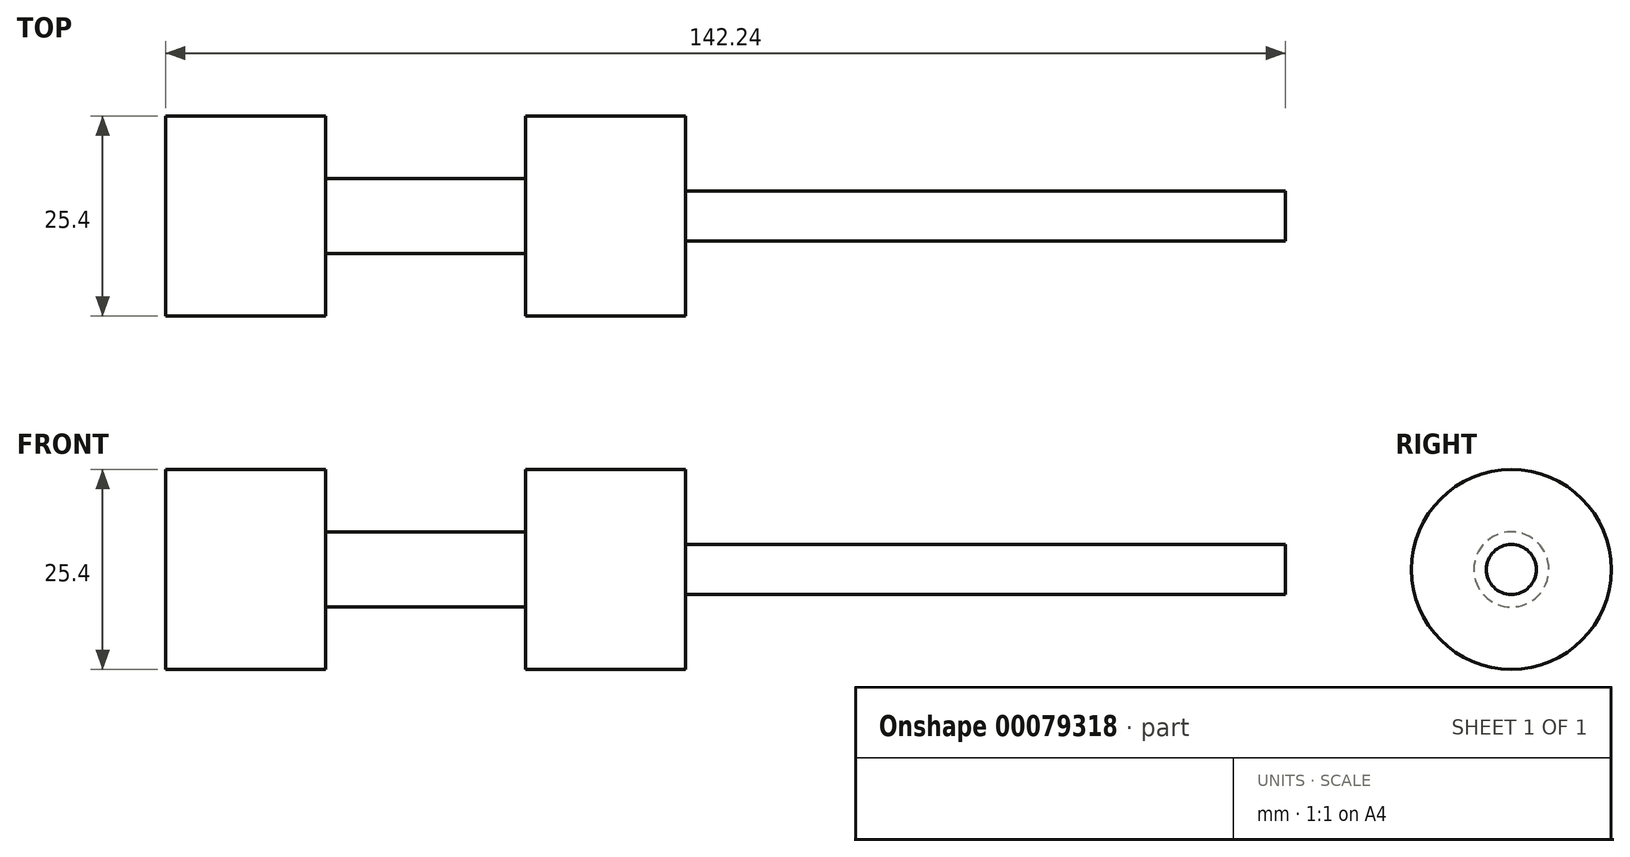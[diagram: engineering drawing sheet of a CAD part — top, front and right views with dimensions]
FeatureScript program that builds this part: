
annotation { "Feature Type Name" : "Feature", "Feature Type Description" : "" }
export const myFeature = defineFeature(function(context is Context, id is Id, definition is map)
    precondition{}
    {
        {
            var Q0;
            Q0=qCreatedBy(makeId("Right.planeOp"),FACE);
            var sketch = newSketch(context, id + "F0", { "sketchPlane" : qUnion([Q0])});
            skCircle(sketch, "E0", {"center": v(0, 0) * mm, "radius": 4.76 * mm});
            skSolve(sketch);
        }
        {
            var Q0;
            Q0 = qSketchRegion(id + "F0", true);
            extrude(context, id + "F1", {"entities" : qUnion([Q0]), "depth" : 12.7 * mm});
        }
        {
            var Q0;
            Q0=makeQuery(id+"F1.opExtrude","CAP_FACE",FACE,{"disambiguationData":[OSD([sQuery(id+"F0.wireOp",EDGE,"E0")])],"isStart":false});
            var sketch = newSketch(context, id + "F2", { "sketchPlane" : qUnion([Q0])});
            skCircle(sketch, "E1", {"center": v(0, 0) * mm, "radius": 12.7 * mm});
            skSolve(sketch);
        }
        {
            var Q0;
            Q0 = qSketchRegion(id + "F2", true);
            extrude(context, id + "F3", {"entities" : qUnion([Q0]), "operationType" : NewBodyOperationType.ADD, "depth" : 20.32 * mm});
        }
        {
            var Q0;
            Q0=makeQuery(id+"F1.opExtrude","SWEPT_BODY",BODY,{"disambiguationData":[OSD([sQuery(id+"F0.wireOp",EDGE,"E0")])]});
            var Q1;
            Q1=qCreatedBy(makeId("Right.planeOp"),FACE);
            mirror(context, id + "F4", {"operationType" : NewBodyOperationType.ADD, "entities" : qUnion([Q0]), "mirrorPlane" : qUnion([Q1])});
        }
        {
            var Q0;
            Q0=makeQuery(id+"F3.opExtrude","CAP_FACE",FACE,{"disambiguationData":[OSD([sQuery(id+"F2.wireOp",EDGE,"E1")])],"isStart":false});
            var sketch = newSketch(context, id + "F5", { "sketchPlane" : qUnion([Q0])});
            skCircle(sketch, "E2", {"center": v(0, 0) * mm, "radius": 3.18 * mm});
            skSolve(sketch);
        }
        {
            var Q0;
            Q0 = qSketchRegion(id + "F5", true);
            extrude(context, id + "F6", {"entities" : qUnion([Q0]), "operationType" : NewBodyOperationType.ADD, "depth" : 76.2 * mm});
        }
    });
